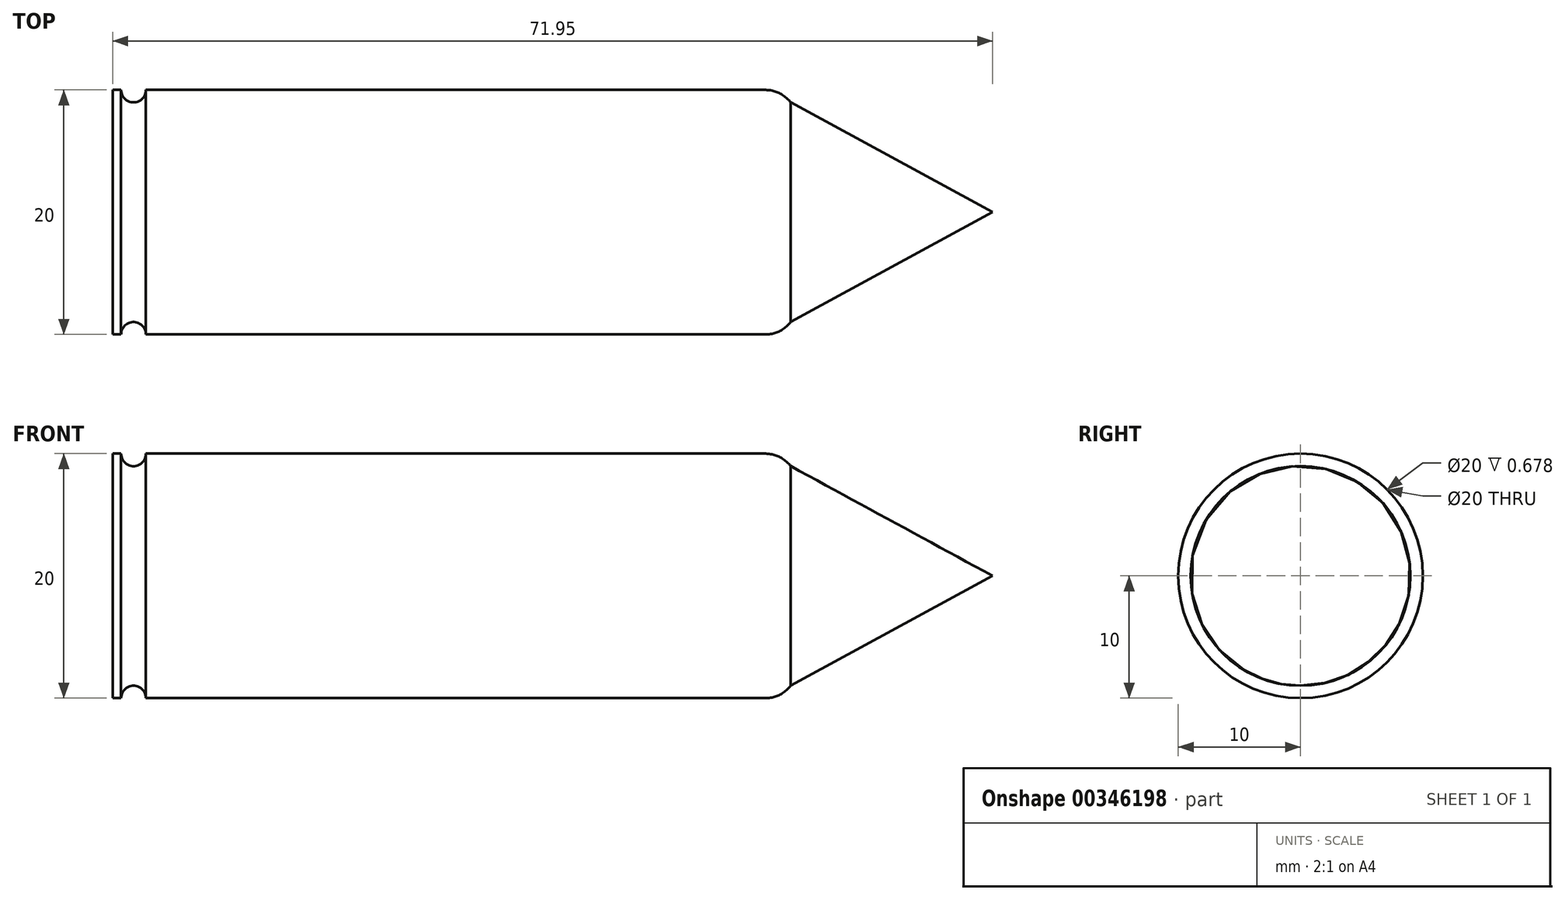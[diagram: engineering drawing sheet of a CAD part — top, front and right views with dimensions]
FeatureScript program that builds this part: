
annotation { "Feature Type Name" : "Feature", "Feature Type Description" : "" }
export const myFeature = defineFeature(function(context is Context, id is Id, definition is map)
    precondition{}
    {
        {
            var Q0;
            Q0=qCreatedBy(makeId("Front.planeOp"),FACE);
            var sketch = newSketch(context, id + "F0", { "sketchPlane" : qUnion([Q0])});
            skArc(sketch, "E0", {"start": v(0.68, 10) * mm, "mid": v(1.7, 8.98) * mm, "end": v(2.71, 10) * mm});
            skLineSegment(sketch, "E1", {"start": v(3.39, 10) * mm, "end": v(53.39, 10) * mm});
            skLineSegment(sketch, "E2.trimOffspring", {"start": v(2.71, 10) * mm, "end": v(3.39, 10) * mm});
            skLineSegment(sketch, "E3", {"start": v(0.68, 10) * mm, "end": v(0, 10) * mm});
            skLineSegment(sketch, "E4", {"start": v(0, 10) * mm, "end": v(0, 0) * mm});
            skArc(sketch, "E5", {"start": v(53.39, 10) * mm, "mid": v(54.53, 9.73) * mm, "end": v(55.42, 8.98) * mm});
            skLineSegment(sketch, "E6", {"start": v(55.42, 8.98) * mm, "end": v(71.95, 0) * mm});
            skSolve(sketch);
        }
        {
            var Q0;
            Q0=qCreatedBy(makeId("Front.planeOp"),FACE);
            var sketch = newSketch(context, id + "F1", { "sketchPlane" : qUnion([Q0])});
            skLineSegment(sketch, "E7", {"start": v(-41.64, 0) * mm, "end": v(-13.31, 0) * mm});
            skSolve(sketch);
        }
        {
            var Q0;
            Q0 = qConstructionFilter(qBodyType(qCreatedBy(id + "F0" ,EDGE), BodyType.WIRE), ConstructionObject.NO);
            var Q1;
            Q1=sQuery(id+"F1.wireOp",EDGE,"E7");
            revolve(context, id + "F2", {"bodyType" : ToolBodyType.SURFACE, "surfaceEntities" : qUnion([Q0]), "axis" : qUnion([Q1]), "revolveType" : RevolveType.FULL});
        }
    });
